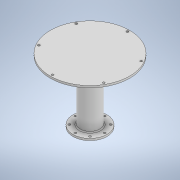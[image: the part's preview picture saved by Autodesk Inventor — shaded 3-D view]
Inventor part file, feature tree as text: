
AUTODESK INVENTOR PART (.ipt)
format: ipt  version: 2021 (Build 250183000, 183)  size: 178,688 bytes
history: native  units: mm
features: sketch x3, revolve x2, hole x2, projected_geometry x2
ambient origin geometry x8: Origin, YZ Plane, XZ Plane, XY Plane, X Axis, Y Axis, Z Axis, Center Point
bodies: Solid1 (feature_tree)
feature tree (9):
  revolve  "Revolution1"  Angle=90.0deg
  revolve  "Revolution2"  [1 undecoded]
  hole  "Hole2"  [1 undecoded]
  hole  "Hole3"  [1 undecoded]
  sketch  "Sketch1"  dims[d2=131.0mm d5=90.0deg]
  projected_geometry  "Projected Loop1"
  sketch  "Sketch4"  dims[d6=42.5mm d7=60.0mm]
  projected_geometry  "Projected Loop4"
  sketch  "Sketch5"  dims[d8=80.0mm d10=360.0deg d12=81.5mm d20=4.5mm d21=8.0mm d22=6.5mm d23=3.0mm d24=90.0deg d25=8.0mm d26=20.594885mm d35=20.0mm d36=4.0mm d37=2.0mm d38=90.0deg d39=35.0mm d40=5.0mm d41=60.0mm d43=360.0deg d45=154.0mm d46=4.5mm d47=6.0mm d48=8.0mm d49=4.0mm d50=90.0deg d51=8.0mm d52=20.594885mm]
note: 3 required parameter values undecoded (feature->parameter linkage not recoverable at this tier; creation-order binding heuristic only, values carry confidence <= 0.55)